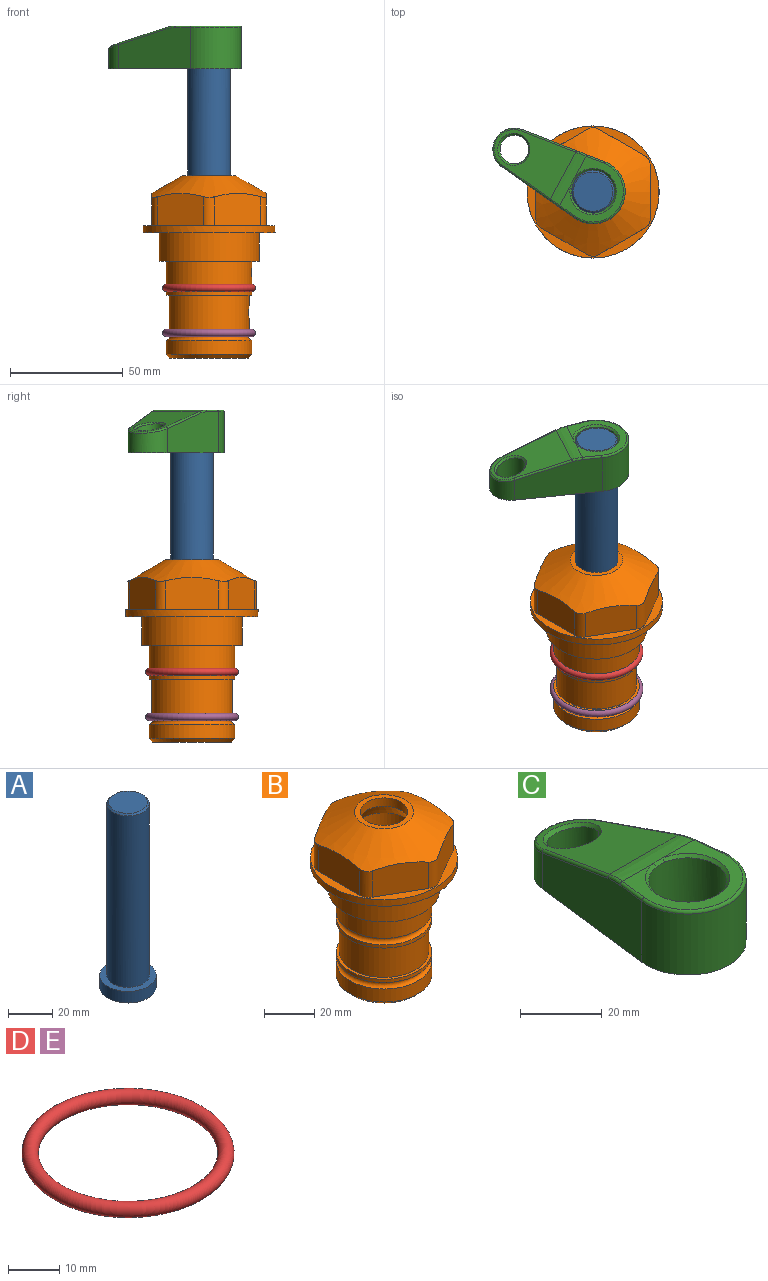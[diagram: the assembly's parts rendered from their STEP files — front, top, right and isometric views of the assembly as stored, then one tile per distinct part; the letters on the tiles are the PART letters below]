
ASSEMBLY  parts=5 mates=4
PART A: 6 faces, bbox 25.4x25.4x101.6 mm
  f0: plane 17.46x17.46mm, normal (0,0,1), area 239.5mm2, adj f5
  f1: plane 25.4x25.4mm, normal (0,0,-1), area 506.7mm2, adj f2
  f2: cylinder r=12.7mm len=25.4mm, axis (0,0,1), area 506.7mm2, adj f1,f3
  f3: plane 25.4x25.4mm, normal (0,0,1), area 221.7mm2, adj f2,f4
  f4: cylinder r=9.53mm len=94.46mm, axis (0,0,1), area 5653mm2, adj f3,f5
  f5: cone r=8.73mm half-angle=45deg, axis (0,0,-1), area 64.4mm2, adj f0,f4
PART B: 36 faces, bbox 58.7x58.7x81 mm
  f0: cylinder r=17.78mm len=35.56mm, axis (0,0,1), area 1670.8mm2, adj f23,f24,f31
  f1: cylinder r=19.05mm len=38.1mm, axis (0,0,1), area 1191.9mm2, adj f26,f27,f30
  f2: plane 58.66x58.66mm, normal (0,0,-1), area 1150.6mm2, adj f3,f28
  f3: cylinder r=29.33mm len=58.66mm, axis (0,0,-1), area 585.1mm2, adj f2,f4
  f4: plane 58.66x58.66mm, normal (0,0,1), area 475.9mm2, adj f3,f5,f6,f7,f8,f9,f10,f11
  f5: plane 20.32x14.34mm, normal (-0.5,0.87,0), area 324.4mm2, adj f4,f15,f16,f17
  f6: plane 20.32x14.34mm, normal (0.5,0.87,0), area 324.4mm2, adj f4,f14,f15,f17
  f7: plane 23.48x14.34mm, normal (1,0,0), area 324.4mm2, adj f4,f13,f14,f17
  f8: plane 20.32x14.34mm, normal (0.5,-0.87,0), area 324.4mm2, adj f4,f12,f13,f17
  f9: plane 20.32x14.34mm, normal (-0.5,-0.87,0), area 324.4mm2, adj f4,f11,f12,f17
  f10: plane 23.48x14.34mm, normal (-1,0,0), area 324.4mm2, adj f4,f11,f16,f17
  f11: cylinder r=5.08mm len=12.85mm, axis (0,0,-1), area 67.2mm2, adj f4,f9,f10,f17
  f12: cylinder r=5.08mm len=12.85mm, axis (0,0,-1), area 67.2mm2, adj f4,f8,f9,f17
  f13: cylinder r=5.08mm len=12.85mm, axis (0,0,-1), area 67.2mm2, adj f4,f7,f8,f17
  f14: cylinder r=5.08mm len=12.85mm, axis (0,0,-1), area 67.2mm2, adj f4,f6,f7,f17
  f15: cylinder r=5.08mm len=12.85mm, axis (0,0,-1), area 67.2mm2, adj f4,f5,f6,f17
  f16: cylinder r=5.08mm len=12.85mm, axis (0,0,-1), area 67.2mm2, adj f4,f5,f10,f17
  f17: cone r=11.73mm half-angle=60deg, axis (0,0,-1), area 2071.8mm2, adj f5,f6,f7,f8,f9,f10,f11,f12
  f18: plane 23.46x23.46mm, normal (0,0,1), area 147.4mm2, adj f17,f35
  f19: plane 34.93x34.93mm, normal (0,0,-1), area 958mm2, adj f29
  f20: cylinder r=19.05mm len=38.1mm, axis (0,0,1), area 760.1mm2, adj f21,f29
  f21: torus R=19.05mm, axis (0,0,1), area 565.3mm2, adj f20,f22
  f22: cylinder r=19.05mm len=38.1mm, axis (0,0,1), area 190mm2, adj f21,f23
  f23: plane 38.1x38.1mm, normal (0,0,1), area 146.9mm2, adj f0,f22
  f24: plane 38.1x38.1mm, normal (0,0,-1), area 146.9mm2, adj f0,f25
  f25: cylinder r=19.05mm len=38.1mm, axis (0,0,1), area 190mm2, adj f24,f26
  f26: torus R=19.05mm, axis (0,0,1), area 565.3mm2, adj f1,f25
  f27: plane 44.45x44.45mm, normal (0,0,-1), area 411.7mm2, adj f1,f28
  f28: cylinder r=22.23mm len=44.45mm, axis (0,0,1), area 1773.5mm2, adj f2,f27
  f29: cone r=19.05mm half-angle=45deg, axis (0,0,1), area 257.5mm2, adj f19,f20
  f30: cylinder r=3.17mm len=6.75mm, axis (-1,0,0), area 128mm2, adj f1,f33
  f31: cylinder r=3.17mm len=6.35mm, axis (-1,0,0), area 102.5mm2, adj f0,f33
  f32: plane 25.4x25.4mm, normal (0,0,1), area 506.7mm2, adj f33
  f33: cylinder r=12.7mm len=66.42mm, axis (0,0,-1), area 5236.2mm2, adj f30,f31,f32,f34
  f34: cone r=9.53mm half-angle=30deg, axis (0,0,-1), area 443.4mm2, adj f33,f35
  f35: cylinder r=9.53mm len=19.05mm, axis (0,0,-1), area 240.9mm2, adj f18,f34
PART C: 31 faces, bbox 31.7x65.5x19.8 mm
  f0: plane 39.12x18.26mm, normal (0.99,0.12,0), area 612.2mm2, adj f1,f4,f7,f11,f13,f15
  f1: cylinder r=9.53mm len=18.91mm, axis (0,0,-1), area 296.1mm2, adj f0,f2,f7,f17
  f2: plane 39.12x18.26mm, normal (-0.99,0.12,0), area 612.2mm2, adj f1,f4,f7,f12,f14,f16
  f3: cylinder r=6.35mm len=12.7mm, axis (0,0,-1), area 362.4mm2, adj f7,f18
  f4: cylinder r=14.29mm len=28.58mm, axis (0,0,-1), area 882.2mm2, adj f0,f2,f7,f10
  f5: cylinder r=9.53mm len=19.05mm, axis (0,0,-1), area 1092.6mm2, adj f7,f19,f20
  f6: plane 26.99x23.69mm, normal (0,0,1), area 216.2mm2, adj f9,f10,f11,f12,f19
  f7: plane 63.5x28.58mm, normal (0,0,-1), area 661.8mm2, adj f0,f1,f2,f3,f4,f5,f22,f23
  f8: plane 33.52x23.6mm, normal (0,0.26,0.97), area 486mm2, adj f9,f15,f16,f17,f18
  f9: cylinder r=19.05mm len=24.72mm, axis (1,0,0), area 120.4mm2, adj f6,f8,f13,f14,f20
  f10: torus R=13.49mm, axis (0,0,1), area 59mm2, adj f4,f6,f11,f12
  f11: cylinder r=0.79mm len=8.67mm, axis (0.12,-0.99,0), area 10.8mm2, adj f0,f6,f10,f13
  f12: cylinder r=0.79mm len=8.67mm, axis (0.12,0.99,0), area 10.8mm2, adj f2,f6,f10,f14
  f13: bspline ~4.95x1.42mm, area 6.1mm2, adj f0,f9,f11,f15
  f14: bspline ~4.95x1.42mm, area 6.1mm2, adj f2,f9,f12,f16
  f15: cylinder r=0.79mm len=25.95mm, axis (0.12,-0.96,0.26), area 32.9mm2, adj f0,f8,f13,f17
  f16: cylinder r=0.79mm len=25.95mm, axis (0.12,0.96,-0.26), area 32.9mm2, adj f2,f8,f14,f17
  f17: bspline ~18.91x8.38mm, area 30mm2, adj f1,f8,f15,f16
  f18: bspline ~14.29x14.29mm, area 48.3mm2, adj f3,f8
  f19: cone r=9.53mm half-angle=45deg, axis (0,0,1), area 66.5mm2, adj f5,f6,f20
  f20: bspline ~3.22x0.96mm, area 3.5mm2, adj f5,f9,f19
  f21: plane 2.75x2.72mm, normal (0,0,-1), area 2.9mm2, adj f23,f25,f28
  f22: plane 23.05x15.88mm, normal (-0.99,-0.12,0), area 323.6mm2, adj f7,f25,f26,f27,f28,f29
  f23: plane 23.05x15.88mm, normal (0.99,-0.12,0), area 323.6mm2, adj f7,f21,f25,f27,f28,f30
  f24: cylinder r=9.53mm len=10.69mm, axis (0,0,-1), area 114.7mm2, adj f7,f27,f29,f30
  f25: cylinder r=12.7mm len=20.59mm, axis (0,0,-1), area 381.1mm2, adj f7,f21,f22,f23,f26,f28
  f26: plane 2.75x2.72mm, normal (0,0,-1), area 2.9mm2, adj f22,f25,f28
  f27: plane 19.72x18.37mm, normal (0,-0.26,-0.97), area 291.8mm2, adj f22,f23,f24,f28,f29,f30
  f28: cylinder r=15.88mm len=19.92mm, axis (1,0,0), area 54.8mm2, adj f21,f22,f23,f25,f26,f27
  f29: cylinder r=1.59mm len=11mm, axis (0,0,-1), area 34.7mm2, adj f7,f22,f24,f27
  f30: cylinder r=1.59mm len=11mm, axis (0,0,-1), area 34.7mm2, adj f7,f23,f24,f27
PART D: 1 faces, bbox 44.7x44.7x3.2 mm
  f0: torus R=19.05mm, axis (0,0,1), area 1193.9mm2
PART E: same geometry as D
PLACE A rot(axis=(0,0,1),61.8deg) t=(0,0,27.55)mm
PLACE B at identity fixed
PLACE C rot(axis=(0,0,1),61.8deg) t=(0,0,28.35)mm
PLACE D at identity
PLACE E t=(0,0,-20)mm
MATE fastened C.f4 <-> A.f2  axis (0,0,-1) through (0,0,91.05)mm
MATE fastened E.f0 <-> B.f0  axis (0,0,1) through (0,0,-44.51)mm
MATE cylindrical A.f2 <-> B.f0  axis (0,0,1) through (0,0,-10.55)mm
MATE fastened D.f0 <-> B.f0  axis (0,0,1) through (0,0,-24.51)mm
